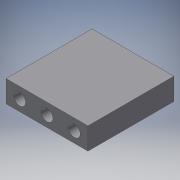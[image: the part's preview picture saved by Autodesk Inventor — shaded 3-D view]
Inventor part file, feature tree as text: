
AUTODESK INVENTOR PART (.ipt)
format: ipt  version: 2019.4 (Build 234330000, 330)  size: 120,320 bytes
history: native  units: mm
features: sketch x2, extrude x1, hole x1, pattern_linear x1, mirror x1
ambient origin geometry x8: Origin, YZ Plane, XZ Plane, XY Plane, X Axis, Y Axis, Z Axis, Center Point
bodies: Solid1 (feature_tree)
feature tree (6):
  extrude  "Extrusion1"  Depth=30.0mm
  hole  "Hole1"  [1 undecoded]
  pattern_linear  "Rectangular Pattern1"  Count1=2 Spacing1=10.0mm
  mirror  "Mirror1"
  sketch  "Sketch1"  dims[d0=8.0mm d1=30.0mm]
  sketch  "Sketch2"  dims[d2=15.75mm d3=0.0mm d4=3.0mm d5=3.88mm d6=6.0mm d7=4.34mm d8=2.0mm d9=1.22173mm d10=7.0mm d11=0.0mm d12=20.0mm d14=10.0mm d15=20.0mm d17=10.0mm d18=15.75mm d19=0.0mm]
note: 1 required parameter value undecoded (feature->parameter linkage not recoverable at this tier; creation-order binding heuristic only, values carry confidence <= 0.55)
